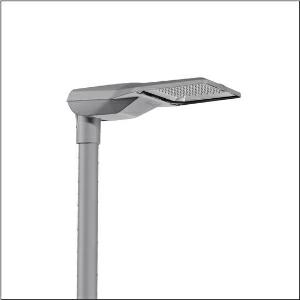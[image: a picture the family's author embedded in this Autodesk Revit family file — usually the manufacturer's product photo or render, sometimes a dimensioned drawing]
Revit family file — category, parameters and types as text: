
# Revit family: streetlight_sl_21_iq_midi___pc-r_5xe3g41g08mb_0911
name_source: partatom
category: Lighting Fixtures
units: mm (PartAtom-declared; Revit-internal decimal feet)

## family parameters
Cut with Voids When Loaded = No
Host = Face
Light Source = No
Part Type = Normal
Room Calculation Point = No
Round Connector Dimension = Use Diameter
Shared = No

## types (1)
- --- (1 x LED, 19370 lm, 146.7 W, 4000K)
    Apparent Load = 147 VA
    CIE Flux Codes = 38 78 98 100 100
    Color Rendering = 70
    Color Temperature = 4000K
    Default Elevation = 1800 mm
    Description = Streetlight SL 21 iQ midi, mast luminaire, primary light control with lens, of PMMA, primary optical cover: cover, of toughened safety glass, transparent, light distribution: PC-R, light emission: direct distribution, primary light characteristic: asymmetric, right, installation type: post-top, side-entry, LED, High Power LED, rated luminous flux: 19.370lm, luminous efficacy: 132lm/W, light colour: 740, colour temperature: 4000K, control: Street-Remote, Auto-Match, Temp-Guard, Lumen-Switch, Night-Set, Smart-Wire, Light-Fading, Desk-Remote (wireless, voltage-free reading and setting of iQ features in the workshop via application-optimized NFC function/RFID function), optimised constant luminous flux control (CLO 2.0), presetting dimming linear, mains connection: 230..240V, AC, 50/60Hz, start of lifetime: 147W, end of service life: 161W, reduction: 62W, luminaire housing, of diecast aluminium, powder-coated, Siteco® metallic grey (DB 702S), corrosivity category C5 mid according to DIN EN ISO 12944, please order mast flange separately, inclination adjustable: 0°, 5°, 10°, 15°, sealing non-destructively replaceable, multi-level sealing system, length: 644mm, width: 335mm, height: 110mm, mast flange for spigot size: 42mm (side-entry): 5XC10008XM4, 60/48mm (side-entry/post-top): 5XC10108XM2, 76/60mm (side-entry/post-top): 5XC10108XM1, protection rating (complete): IP66, insulation class (complete): insulation class II (safety insulation), certification: CE, ENEC, ENEC+, VDE, impact resistance: IK09, permissible operating ambient temperature for outdoor applications: -40..+50°C, standard-compliant lighting for roads and squares, packaging unit: 1 piece

Light Distribution: PC-R
    Height = 111 mm
    Lamp = 1 x LED
    Lamp Light Flux = 19370 lm
    Lamp Power = 146.7 W
    Lamp count = 1
    Length = 644 mm
    Luminous efficacy = 132 lm/W
    Manufacturer = Siteco
    ModVariant = No
    Model = 5XE3G41G08MB
    Number of Poles = 1
    OnlyDefault = Yes
    Power Factor = 1
    Product Name = Streetlight SL 21 iQ midi | PC-R
    Product group = mast luminaire | pylon top
    ProductGroupID = 6100
    Protection Class = Protection class II
    Protection Degree = IP 66
    RLX_Detail_Level = 1
    RLX_Emergency_Light_Flux = 0 lm
    RLX_Emergency_Type = 0
    RLX_Emergency_Type_DB = No
    RlxData = <blob elided: 93193 chars, md5=3f294d6b>
    Socket = socket
    Standby Power = 0 W
    System Light Flux = 19370 lm
    System Power = 147 W
    Type Comments = factory setting: luminous flux: 100 % | dim-lin: 254 | 753 mA
    Type Image = l_1004298.jpg
    URL = http://relux.com
    VarID = @adj_005105
    Voltage = 0 V
    Weight = 0.00 kg
    Width = 336 mm

## geometry (parser evidence)
native form markers: Blend x4, Sweep x11
no freeform markers — native parametric forms only
